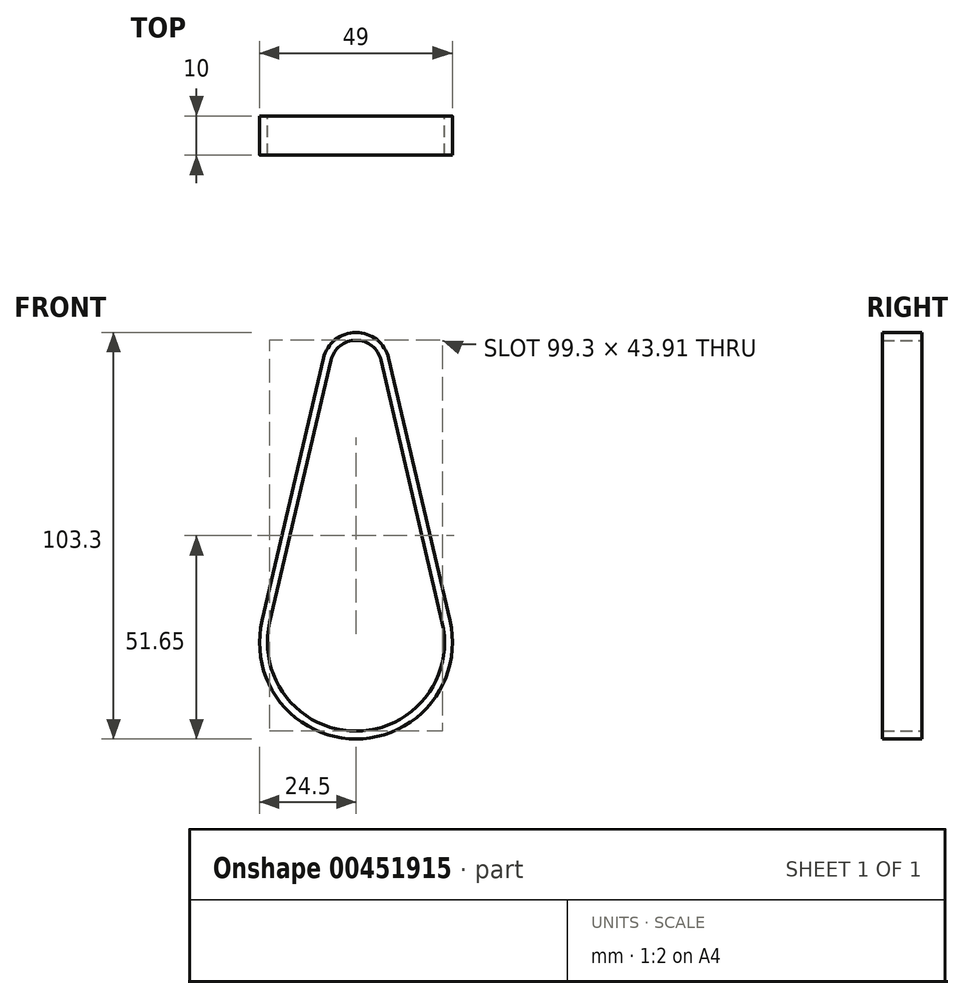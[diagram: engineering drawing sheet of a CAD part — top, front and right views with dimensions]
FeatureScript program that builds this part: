
annotation { "Feature Type Name" : "Feature", "Feature Type Description" : "" }
export const myFeature = defineFeature(function(context is Context, id is Id, definition is map)
    precondition{}
    {
        {
            var Q0;
            Q0=qCreatedBy(makeId("Front.planeOp"),FACE);
            var sketch = newSketch(context, id + "F0", { "sketchPlane" : qUnion([Q0])});
            skArc(sketch, "E0", {"start": v(-21.9, 5.12) * mm, "mid": v(0, -22.5) * mm, "end": v(21.9, 5.12) * mm});
            skArc(sketch, "E1", {"start": v(6.33, 71.78) * mm, "mid": v(0, 76.8) * mm, "end": v(-6.33, 71.78) * mm});
            skLineSegment(sketch, "E2", {"start": v(-6.33, 71.78) * mm, "end": v(-21.9, 5.12) * mm});
            skLineSegment(sketch, "E3", {"start": v(6.33, 71.78) * mm, "end": v(21.9, 5.12) * mm});
            skArc(sketch, "E4.0", {"start": v(8.28, 72.23) * mm, "mid": v(0, 78.8) * mm, "end": v(-8.28, 72.23) * mm});
            skLineSegment(sketch, "E4.1", {"start": v(8.28, 72.23) * mm, "end": v(23.86, 5.58) * mm});
            skArc(sketch, "E4.2", {"start": v(-23.86, 5.58) * mm, "mid": v(0, -24.5) * mm, "end": v(23.86, 5.58) * mm});
            skLineSegment(sketch, "E4.3", {"start": v(-8.28, 72.23) * mm, "end": v(-23.86, 5.58) * mm});
            skLineSegment(sketch, "E5.0", {"start": v(-7.3, 72) * mm, "end": v(-22.88, 5.35) * mm, "construction": true});
            skArc(sketch, "E5.1", {"start": v(7.3, 72) * mm, "mid": v(0, 77.8) * mm, "end": v(-7.3, 72) * mm, "construction": true});
            skLineSegment(sketch, "E5.2", {"start": v(7.3, 72) * mm, "end": v(22.88, 5.35) * mm, "construction": true});
            skArc(sketch, "E5.3", {"start": v(-22.88, 5.35) * mm, "mid": v(0, -23.5) * mm, "end": v(22.88, 5.35) * mm, "construction": true});
            skSolve(sketch);
        }
        {
            var Q0;
            Q0=qSketchRegion(id+"F0",true);
            extrude(context, id + "F1", {"entities" : qUnion([Q0]), "depth" : 10 * mm});
        }
    });
